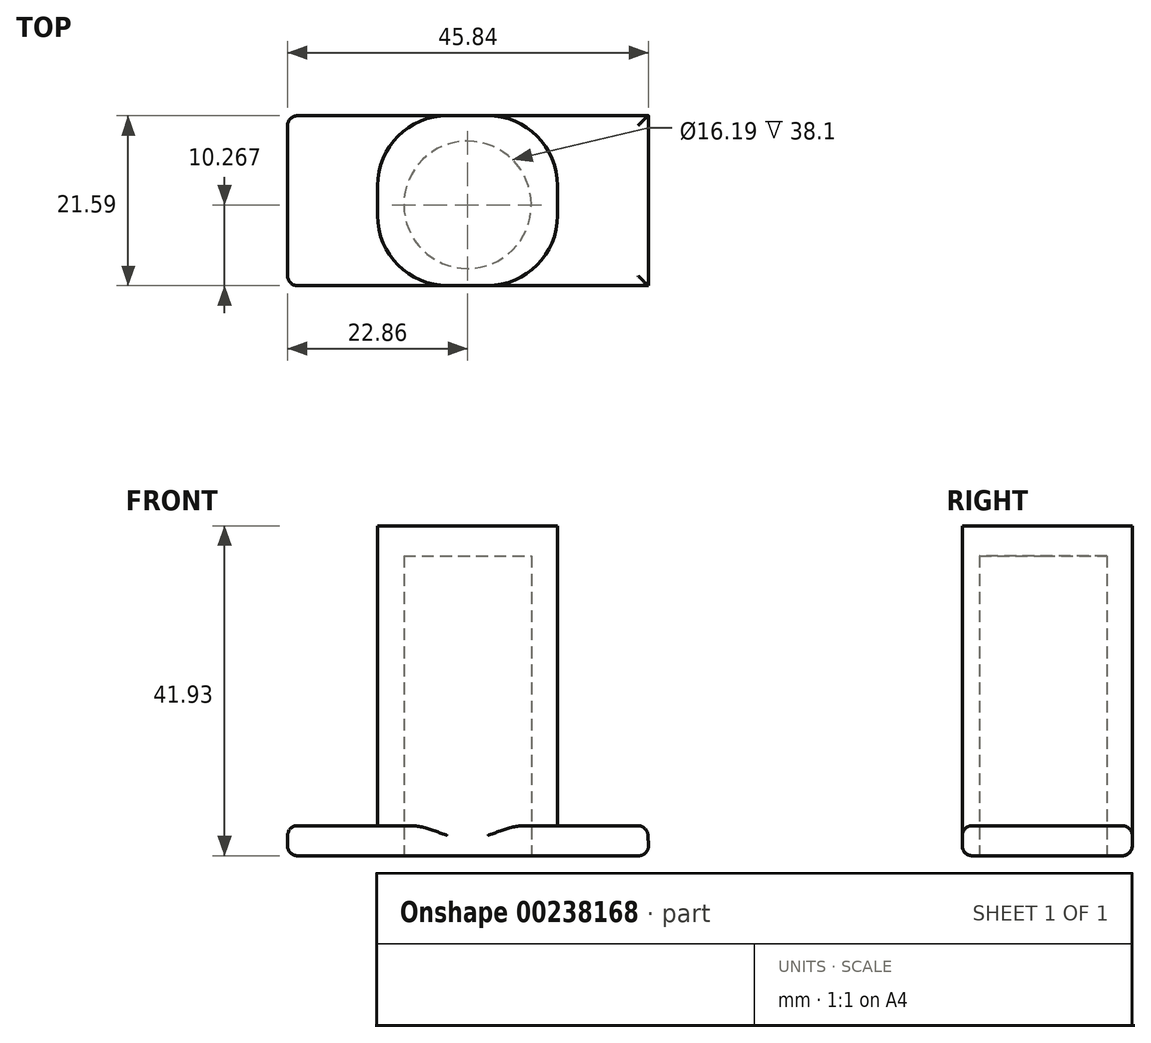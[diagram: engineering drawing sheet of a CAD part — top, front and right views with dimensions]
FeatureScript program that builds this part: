
annotation { "Feature Type Name" : "Feature", "Feature Type Description" : "" }
export const myFeature = defineFeature(function(context is Context, id is Id, definition is map)
    precondition{}
    {
        {
            var Q0;
            Q0=qCreatedBy(makeId("Front.planeOp"),FACE);
            var sketch = newSketch(context, id + "F0", { "sketchPlane" : qUnion([Q0])});
            skLineSegment(sketch, "E0", {"start": v(-22.86, 0) * mm, "end": v(0, 0) * mm});
            skLineSegment(sketch, "E1", {"start": v(0, 0) * mm, "end": v(22.86, 0) * mm});
            skLineSegment(sketch, "E2", {"start": v(-11.43, 0) * mm, "end": v(-11.43, 38.1) * mm});
            skLineSegment(sketch, "E3", {"start": v(11.43, 0) * mm, "end": v(11.43, 38.1) * mm});
            skLineSegment(sketch, "E4", {"start": v(-11.43, 38.1) * mm, "end": v(11.43, 38.1) * mm});
            skLineSegment(sketch, "E5", {"start": v(-22.86, 0) * mm, "end": v(-22.86, -3.83) * mm});
            skLineSegment(sketch, "E6", {"start": v(-22.86, -3.83) * mm, "end": v(23.05, -3.83) * mm});
            skLineSegment(sketch, "E7", {"start": v(23.05, -3.83) * mm, "end": v(22.86, 0) * mm});
            skSolve(sketch);
        }
        {
            var Q0;
            {var subQ6=sQuery(id+"F0.wireOp",EDGE,"E5");Q0=makeQuery(id+"F0.imprint","IMPRINT",FACE,{"disambiguationData":[TD([[makeQuery(id+"F0.imprint","IMPRINT",EDGE,{"derivedFrom":subQ6}),1.0]])]});}
            var Q1;
            {var subQ1=sQuery(id+"F0.wireOp",EDGE,"E2");Q1=makeQuery(id+"F0.imprint","IMPRINT",FACE,{"disambiguationData":[TD([[makeQuery(id+"F0.imprint","IMPRINT",EDGE,{"derivedFrom":subQ1}),-1.0]])]});}
            extrude(context, id + "F1", {"entities" : qUnion([Q0, Q1]), "depth" : 21.59 * mm});
        }
        {
            var Q0;
            Q0=makeQuery(id+"F1.opExtrude","CAP_EDGE",EDGE,{"disambiguationData":[OSD([sQuery(id+"F0.wireOp",EDGE,"E3")])],"isStart":false});
            fillet(context, id + "F2", {"entities" : qUnion([Q0]), "radius" : 8.9 * mm, "tangentPropagation" : true, "allowEdgeOverflow" : false});
        }
        {
            var Q0;
            Q0=makeQuery(id+"F1.opExtrude","CAP_EDGE",EDGE,{"disambiguationData":[OSD([sQuery(id+"F0.wireOp",EDGE,"E2")])],"isStart":false});
            var Q1;
            Q1=makeQuery(id+"F1.opExtrude","CAP_EDGE",EDGE,{"disambiguationData":[OSD([sQuery(id+"F0.wireOp",EDGE,"E3")])],"isStart":true});
            var Q2;
            Q2=makeQuery(id+"F1.opExtrude","CAP_EDGE",EDGE,{"disambiguationData":[OSD([sQuery(id+"F0.wireOp",EDGE,"E2")])],"isStart":true});
            fillet(context, id + "F3", {"entities" : qUnion([Q0, Q1, Q2]), "radius" : 8.9 * mm, "tangentPropagation" : true, "allowEdgeOverflow" : false});
        }
        {
            var Q0;
            Q0=makeQuery(id+"F1.opExtrude","SWEPT_EDGE",EDGE,{"disambiguationData":[OSD([sQuery(id+"F0.wireOp",EDGE,"E0"),sQuery(id+"F0.wireOp",EDGE,"E5")])]});
            fillet(context, id + "F4", {"entities" : qUnion([Q0]), "radius" : 1.27 * mm, "tangentPropagation" : true, "allowEdgeOverflow" : false});
        }
        {
            var Q0;
            Q0=makeQuery(id+"F1.opExtrude","SWEPT_EDGE",EDGE,{"disambiguationData":[OSD([sQuery(id+"F0.wireOp",EDGE,"E5"),sQuery(id+"F0.wireOp",EDGE,"E6")])]});
            fillet(context, id + "F5", {"entities" : qUnion([Q0]), "radius" : 1.27 * mm, "tangentPropagation" : true, "allowEdgeOverflow" : false});
        }
        {
            var Q0;
            Q0=makeQuery(id+"F1.opExtrude","CAP_EDGE",EDGE,{"disambiguationData":[OSD([sQuery(id+"F0.wireOp",EDGE,"E0")])],"isStart":true});
            var Q1;
            Q1=makeQuery(id+"F1.opExtrude","CAP_EDGE",EDGE,{"disambiguationData":[OSD([sQuery(id+"F0.wireOp",EDGE,"E6")])],"isStart":true});
            var Q2;
            Q2=makeQuery(id+"F1.opExtrude","CAP_EDGE",EDGE,{"disambiguationData":[OSD([sQuery(id+"F0.wireOp",EDGE,"E1")])],"isStart":true});
            var Q3;
            Q3=makeQuery(id+"F1.opExtrude","SWEPT_EDGE",EDGE,{"disambiguationData":[OSD([sQuery(id+"F0.wireOp",EDGE,"E1"),sQuery(id+"F0.wireOp",EDGE,"E7")])]});
            var Q4;
            Q4=makeQuery(id+"F1.opExtrude","SWEPT_EDGE",EDGE,{"disambiguationData":[OSD([sQuery(id+"F0.wireOp",EDGE,"E6"),sQuery(id+"F0.wireOp",EDGE,"E7")])]});
            var Q5;
            Q5=makeQuery(id+"F1.opExtrude","CAP_EDGE",EDGE,{"disambiguationData":[OSD([sQuery(id+"F0.wireOp",EDGE,"E1")])],"isStart":false});
            var Q6;
            Q6=makeQuery(id+"F1.opExtrude","CAP_EDGE",EDGE,{"disambiguationData":[OSD([sQuery(id+"F0.wireOp",EDGE,"E6")])],"isStart":false});
            var Q7;
            Q7=makeQuery(id+"F1.opExtrude","CAP_EDGE",EDGE,{"disambiguationData":[OSD([sQuery(id+"F0.wireOp",EDGE,"E0")])],"isStart":false});
            fillet(context, id + "F6", {"entities" : qUnion([Q0, Q1, Q2, Q3, Q4, Q5, Q6, Q7]), "radius" : 1.27 * mm, "tangentPropagation" : true, "allowEdgeOverflow" : false});
        }
        {
            var Q0;
            Q0=makeQuery(id+"F1.opExtrude","SWEPT_FACE",FACE,{"disambiguationData":[OSD([sQuery(id+"F0.wireOp",EDGE,"E6")])]});
            var sketch = newSketch(context, id + "F7", { "sketchPlane" : qUnion([Q0])});
            skCircle(sketch, "E8", {"center": v(0, 11.32) * mm, "radius": 8.1 * mm});
            skSolve(sketch);
        }
        {
            var Q0;
            Q0=makeQuery(id+"F7.imprint","IMPRINT",FACE,{"disambiguationData":[TD([[makeQuery(id+"F7.imprint","IMPRINT",EDGE,{"derivedFrom":sQuery(id+"F7.wireOp",EDGE,"E8")}),1.0]])]});
            extrude(context, id + "F8", {"entities" : qUnion([Q0]), "operationType" : NewBodyOperationType.REMOVE, "oppositeDirection" : true, "depth" : 38.1 * mm});
        }
    });
